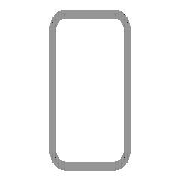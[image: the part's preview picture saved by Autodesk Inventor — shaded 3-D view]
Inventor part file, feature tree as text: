
AUTODESK INVENTOR PART (.ipt)
format: ipt  version: 2025 (Build 290162010, 162A)  size: 129,024 bytes
history: native  units: mm (DEFAULTED — no unit token found)
features: other x3, sketch x1, plane x1
ambient origin geometry x8: Origin, YZ Plane, XZ Plane, XY Plane, X Axis, Y Axis, Z Axis, Center Point
bodies: Solid1 (feature_tree), Body (feature_tree)
feature tree (5):
  other  "Driven Length"
  other  "Start plane"
  other  "End plane"
  sketch  "Sketch3"  dims[d3=2000.0mm d4=0.0mm d7=6.0mm d9=40.0mm d11=60.0mm d12=3.0mm d13=-0.0mm d14=2000.0mm d15=20.0mm d16=30.0mm d17=90.0deg d18=2000.0mm]
  plane  "Work Plane3"
